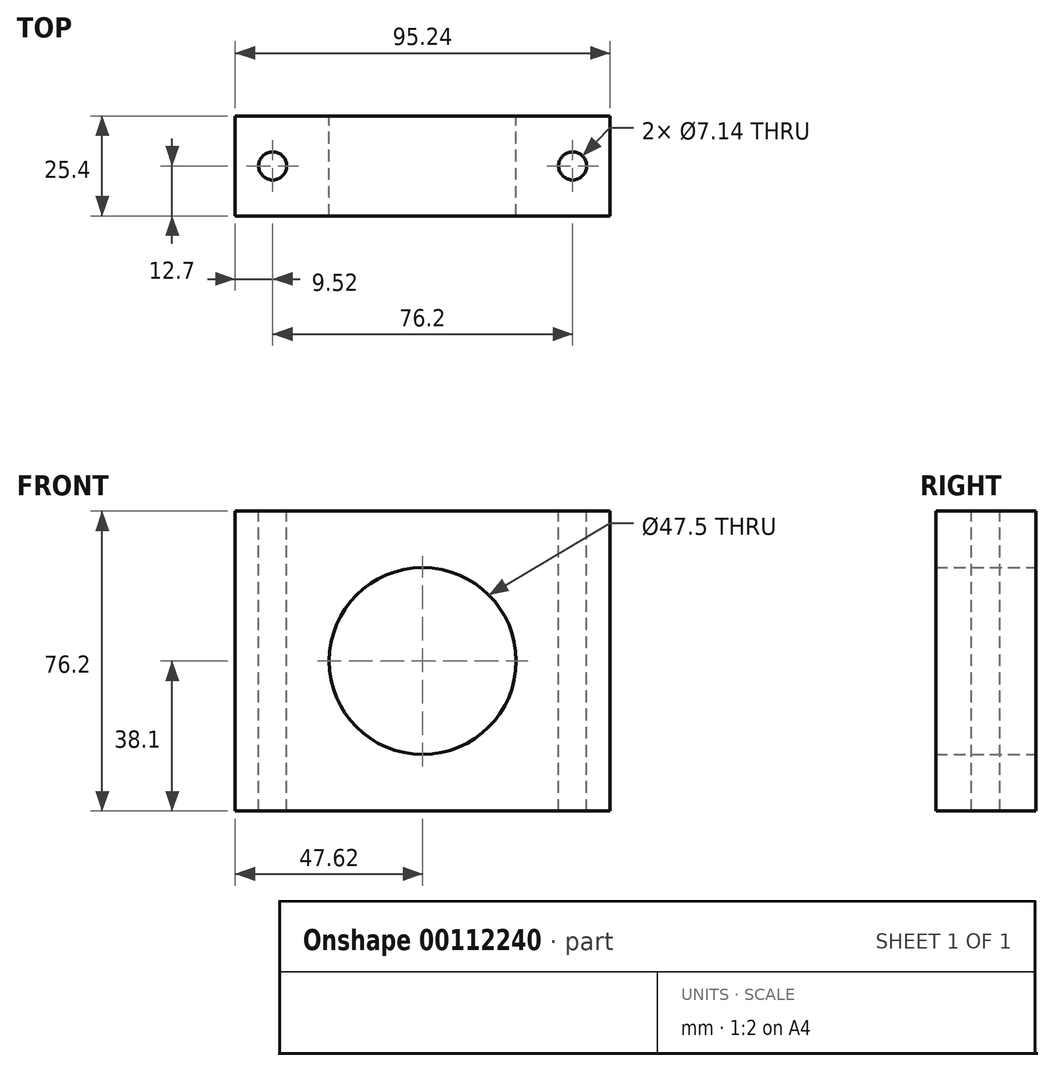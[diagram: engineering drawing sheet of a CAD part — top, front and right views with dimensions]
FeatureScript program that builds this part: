
annotation { "Feature Type Name" : "Feature", "Feature Type Description" : "" }
export const myFeature = defineFeature(function(context is Context, id is Id, definition is map)
    precondition{}
    {
        {
            var Q0;
            Q0=qCreatedBy(makeId("Front.planeOp"),FACE);
            var sketch = newSketch(context, id + "F0", { "sketchPlane" : qUnion([Q0])});
            skLineSegment(sketch, "E0.bottom", {"start": v(47.63, 38.1) * mm, "end": v(-47.62, 38.1) * mm});
            skLineSegment(sketch, "E0.top", {"start": v(47.62, -38.1) * mm, "end": v(-47.63, -38.1) * mm});
            skLineSegment(sketch, "E0.left", {"start": v(47.63, 38.1) * mm, "end": v(47.62, -38.1) * mm});
            skLineSegment(sketch, "E0.right", {"start": v(-47.62, 38.1) * mm, "end": v(-47.63, -38.1) * mm});
            skPoint(sketch, "E0.middle", {"position": v(0, 0) * mm});
            skCircle(sketch, "E1", {"center": v(0, 0) * mm, "radius": 23.75 * mm});
            skSolve(sketch);
        }
        {
            var Q0;
            Q0=makeQuery(id+"F0.imprint","IMPRINT",FACE,{"disambiguationData":[TD([[makeQuery(id+"F0.imprint","IMPRINT",EDGE,{"derivedFrom":sQuery(id+"F0.wireOp",EDGE,"E0.bottom")}),1.0]])]});
            extrude(context, id + "F1", {"entities" : qUnion([Q0]), "depth" : 25.4 * mm});
        }
        {
            var Q0;
            Q0=makeQuery(id+"F1.opExtrude","SWEPT_FACE",FACE,{"disambiguationData":[OSD([sQuery(id+"F0.wireOp",EDGE,"E0.bottom")])]});
            var sketch = newSketch(context, id + "F2", { "sketchPlane" : qUnion([Q0])});
            skLineSegment(sketch, "E2.bottom", {"start": v(-47.62, 0) * mm, "end": v(-38.1, 0) * mm, "construction": true});
            skLineSegment(sketch, "E2.top", {"start": v(-47.62, -12.7) * mm, "end": v(-38.1, -12.7) * mm, "construction": true});
            skLineSegment(sketch, "E2.left", {"start": v(-47.62, 0) * mm, "end": v(-47.62, -12.7) * mm, "construction": true});
            skLineSegment(sketch, "E2.right", {"start": v(-38.1, 0) * mm, "end": v(-38.1, -12.7) * mm, "construction": true});
            skCircle(sketch, "E3", {"center": v(-38.1, -12.7) * mm, "radius": 3.57 * mm});
            skLineSegment(sketch, "E4.bottom", {"start": v(47.63, 0) * mm, "end": v(38.1, 0) * mm, "construction": true});
            skLineSegment(sketch, "E4.top", {"start": v(47.63, -12.7) * mm, "end": v(38.1, -12.7) * mm, "construction": true});
            skLineSegment(sketch, "E4.left", {"start": v(47.63, 0) * mm, "end": v(47.63, -12.7) * mm, "construction": true});
            skLineSegment(sketch, "E4.right", {"start": v(38.1, 0) * mm, "end": v(38.1, -12.7) * mm, "construction": true});
            skCircle(sketch, "E5", {"center": v(38.1, -12.7) * mm, "radius": 3.57 * mm});
            skSolve(sketch);
        }
        {
            var Q0;
            Q0=makeQuery(id+"F2.imprint","IMPRINT",FACE,{"disambiguationData":[TD([[makeQuery(id+"F2.imprint","IMPRINT",EDGE,{"derivedFrom":sQuery(id+"F2.wireOp",EDGE,"E5")}),1.0]])]});
            var Q1;
            Q1=makeQuery(id+"F2.imprint","IMPRINT",FACE,{"disambiguationData":[TD([[makeQuery(id+"F2.imprint","IMPRINT",EDGE,{"derivedFrom":sQuery(id+"F2.wireOp",EDGE,"E3")}),1.0]])]});
            extrude(context, id + "F3", {"entities" : qUnion([Q0, Q1]), "operationType" : NewBodyOperationType.REMOVE, "oppositeDirection" : true, "depth" : 76.2 * mm});
        }
    });
